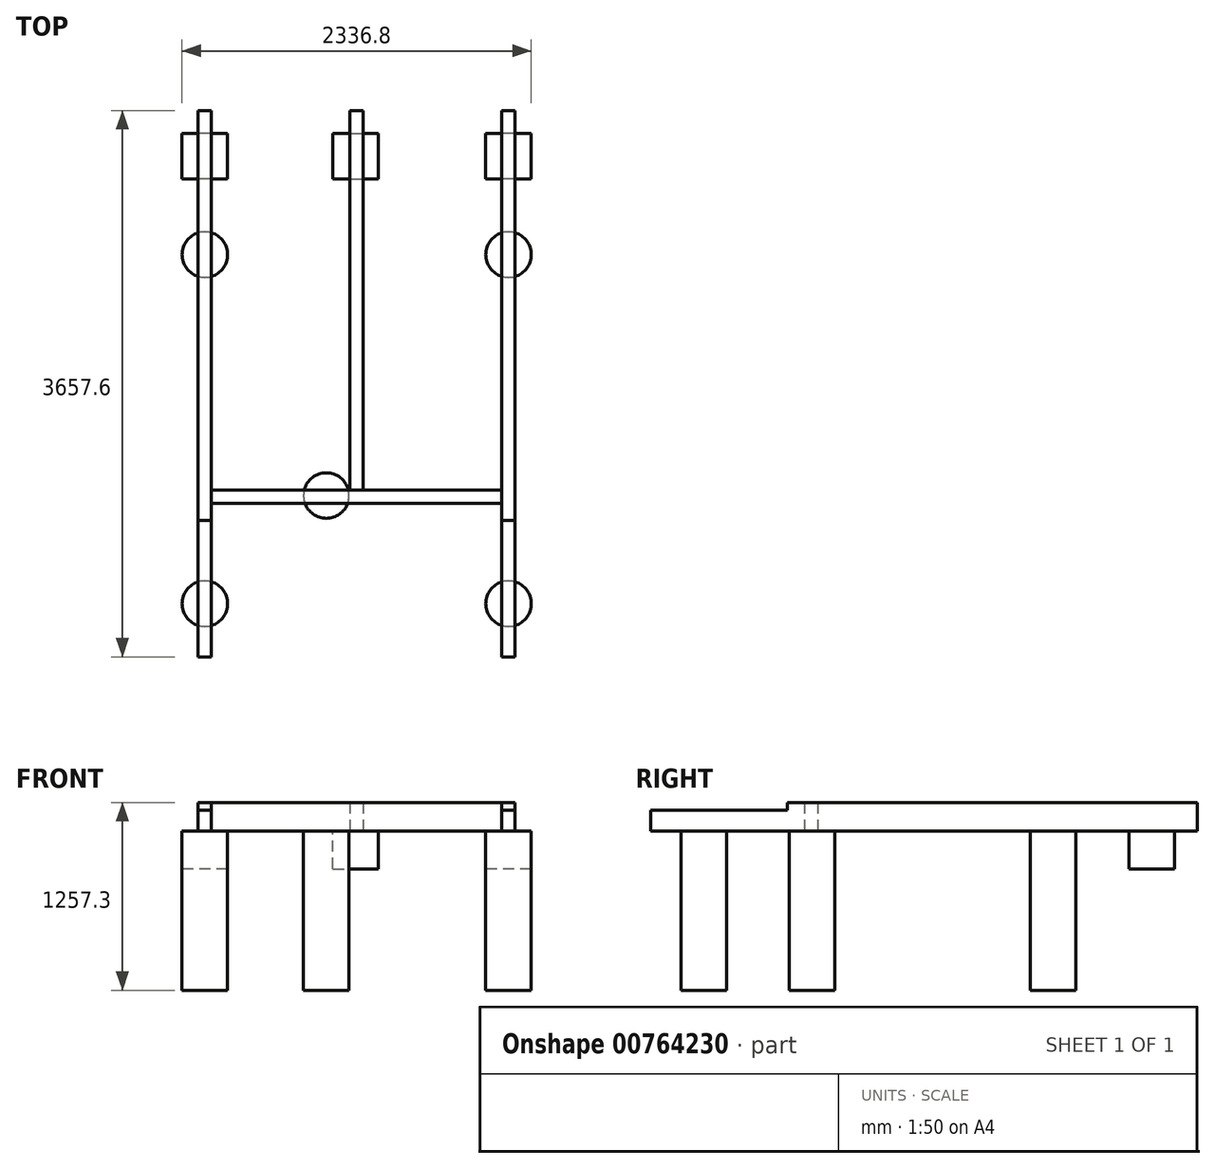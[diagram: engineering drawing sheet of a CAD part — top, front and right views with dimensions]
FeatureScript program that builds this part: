
annotation { "Feature Type Name" : "Feature", "Feature Type Description" : "" }
export const myFeature = defineFeature(function(context is Context, id is Id, definition is map)
    precondition{}
    {
        {
            var Q0;
            Q0=qCreatedBy(makeId("Top.planeOp"),FACE);
            var sketch = newSketch(context, id + "F0", { "sketchPlane" : qUnion([Q0])});
            skLineSegment(sketch, "E0.bottom", {"start": v(-1016, 1828.8) * mm, "end": v(1016, 1828.8) * mm, "construction": true});
            skLineSegment(sketch, "E0.top", {"start": v(-1016, -1828.8) * mm, "end": v(1016, -1828.8) * mm, "construction": true});
            skLineSegment(sketch, "E0.left", {"start": v(-1016, 1828.8) * mm, "end": v(-1016, -1828.8) * mm, "construction": true});
            skLineSegment(sketch, "E0.right", {"start": v(1016, 1828.8) * mm, "end": v(1016, -1828.8) * mm, "construction": true});
            skPoint(sketch, "E0.middle", {"position": v(0, 0) * mm});
            skLineSegment(sketch, "E1.left", {"start": v(-1034.42, -1828.8) * mm, "end": v(-1034.42, -1828.8) * mm});
            skLineSegment(sketch, "E1.right", {"start": v(-997.58, -1828.8) * mm, "end": v(-997.58, -1828.8) * mm});
            skPoint(sketch, "E1.middle", {"position": v(-1016, -1828.8) * mm});
            skPoint(sketch, "E2", {"position": v(1016, 1828.8) * mm});
            skPoint(sketch, "E3", {"position": v(1016, -1828.8) * mm});
            skPoint(sketch, "E4", {"position": v(0, 1828.8) * mm});
            skPoint(sketch, "E5", {"position": v(0, -1828.8) * mm});
            skPoint(sketch, "E6", {"position": v(-1016, 1828.8) * mm});
            skLineSegment(sketch, "E7.bottom", {"start": v(-971.55, -1828.8) * mm, "end": v(-1060.45, -1828.8) * mm});
            skLineSegment(sketch, "E7.top", {"start": v(-971.55, 1828.8) * mm, "end": v(-1060.45, 1828.8) * mm});
            skLineSegment(sketch, "E7.left", {"start": v(-971.55, -1828.8) * mm, "end": v(-971.55, 1828.8) * mm});
            skLineSegment(sketch, "E7.right", {"start": v(-1060.45, -1828.8) * mm, "end": v(-1060.45, 1828.8) * mm});
            skPoint(sketch, "E7.middle", {"position": v(-1016, 0) * mm});
            skPoint(sketch, "E8", {"position": v(1016, 0) * mm});
            skLineSegment(sketch, "E9.bottom", {"start": v(971.55, 1828.8) * mm, "end": v(1060.45, 1828.8) * mm});
            skLineSegment(sketch, "E9.top", {"start": v(971.55, -1828.8) * mm, "end": v(1060.45, -1828.8) * mm});
            skLineSegment(sketch, "E9.left", {"start": v(971.55, 1828.8) * mm, "end": v(971.55, -1828.8) * mm});
            skLineSegment(sketch, "E9.right", {"start": v(1060.45, 1828.8) * mm, "end": v(1060.45, -1828.8) * mm});
            skPoint(sketch, "E10.positionSnap0", {"position": v(1060.45, 0) * mm});
            skLineSegment(sketch, "E11.bottom", {"start": v(-44.45, 1828.8) * mm, "end": v(44.45, 1828.8) * mm});
            skLineSegment(sketch, "E11.top", {"start": v(-44.45, -711.2) * mm, "end": v(44.45, -711.2) * mm});
            skLineSegment(sketch, "E11.left", {"start": v(-44.45, 1828.8) * mm, "end": v(-44.45, -711.2) * mm});
            skLineSegment(sketch, "E11.right", {"start": v(44.45, 1828.8) * mm, "end": v(44.45, -711.2) * mm});
            skLineSegment(sketch, "E12.bottom", {"start": v(-971.55, -711.2) * mm, "end": v(971.55, -711.2) * mm});
            skLineSegment(sketch, "E12.top", {"start": v(-971.55, -800.1) * mm, "end": v(971.55, -800.1) * mm});
            skLineSegment(sketch, "E12.left", {"start": v(-971.55, -711.2) * mm, "end": v(-971.55, -800.1) * mm});
            skLineSegment(sketch, "E12.right", {"start": v(971.55, -711.2) * mm, "end": v(971.55, -800.1) * mm});
            skSolve(sketch);
        }
        {
            var Q0;
            Q0=makeQuery(id+"F0.imprint","IMPRINT",FACE,{"disambiguationData":[TD([[makeQuery(id+"F0.imprint","IMPRINT",EDGE,{"derivedFrom":sQuery(id+"F0.wireOp",EDGE,"E7.bottom")}),-1.0]])]});
            extrude(context, id + "F1", {"entities" : qUnion([Q0]), "depth" : 190.5 * mm, "offsetDistance" : 25.4 * mm});
        }
        {
            var Q0;
            Q0=makeQuery(id+"F0.imprint","IMPRINT",FACE,{"disambiguationData":[TD([[makeQuery(id+"F0.imprint","IMPRINT",EDGE,{"derivedFrom":sQuery(id+"F0.wireOp",EDGE,"E9.bottom")}),-1.0]])]});
            extrude(context, id + "F2", {"entities" : qUnion([Q0]), "depth" : 190.5 * mm, "offsetDistance" : 25.4 * mm});
        }
        {
            var Q0;
            Q0=makeQuery(id+"F0.imprint","IMPRINT",FACE,{"disambiguationData":[TD([[makeQuery(id+"F0.imprint","IMPRINT",EDGE,{"derivedFrom":sQuery(id+"F0.wireOp",EDGE,"E11.bottom")}),-1.0]])]});
            extrude(context, id + "F3", {"entities" : qUnion([Q0]), "depth" : 190.5 * mm, "offsetDistance" : 25.4 * mm});
        }
        {
            var Q0;
            Q0=makeQuery(id+"F2.opExtrude","SWEPT_FACE",FACE,{"disambiguationData":[OSD([sQuery(id+"F0.wireOp",EDGE,"E9.right")])]});
            var sketch = newSketch(context, id + "F4", { "sketchPlane" : qUnion([Q0])});
            skLineSegment(sketch, "E13.bottom", {"start": v(-1828.8, 190.5) * mm, "end": v(-914.4, 190.5) * mm});
            skLineSegment(sketch, "E13.top", {"start": v(-1828.8, 139.7) * mm, "end": v(-914.4, 139.7) * mm});
            skLineSegment(sketch, "E13.left", {"start": v(-1828.8, 190.5) * mm, "end": v(-1828.8, 139.7) * mm});
            skLineSegment(sketch, "E13.right", {"start": v(-914.4, 190.5) * mm, "end": v(-914.4, 139.7) * mm});
            skSolve(sketch);
        }
        {
            var Q0;
            Q0=makeQuery(id+"F1.opExtrude","SWEPT_FACE",FACE,{"disambiguationData":[OSD([sQuery(id+"F0.wireOp",EDGE,"E7.right")])]});
            var sketch = newSketch(context, id + "F5", { "sketchPlane" : qUnion([Q0])});
            skLineSegment(sketch, "E14.bottom", {"start": v(1828.8, 190.5) * mm, "end": v(914.4, 190.5) * mm});
            skLineSegment(sketch, "E14.top", {"start": v(1828.8, 139.7) * mm, "end": v(914.4, 139.7) * mm});
            skLineSegment(sketch, "E14.left", {"start": v(1828.8, 190.5) * mm, "end": v(1828.8, 139.7) * mm});
            skLineSegment(sketch, "E14.right", {"start": v(914.4, 190.5) * mm, "end": v(914.4, 139.7) * mm});
            skSolve(sketch);
        }
        {
            var Q0;
            Q0=makeQuery(id+"F5.imprint","IMPRINT",FACE,{"disambiguationData":[TD([[makeQuery(id+"F5.imprint","IMPRINT",EDGE,{"derivedFrom":sQuery(id+"F5.wireOp",EDGE,"E14.bottom")}),1.0]])]});
            extrude(context, id + "F6", {"entities" : qUnion([Q0]), "operationType" : NewBodyOperationType.REMOVE, "endBound" : BoundingType.THROUGH_ALL, "oppositeDirection" : true, "depth" : 25.4 * mm, "offsetDistance" : 25.4 * mm});
        }
        {
            var Q0;
            Q0=makeQuery(id+"F4.imprint","IMPRINT",FACE,{"disambiguationData":[TD([[makeQuery(id+"F4.imprint","IMPRINT",EDGE,{"derivedFrom":sQuery(id+"F4.wireOp",EDGE,"E13.bottom")}),1.0]])]});
            extrude(context, id + "F7", {"entities" : qUnion([Q0]), "operationType" : NewBodyOperationType.REMOVE, "endBound" : BoundingType.THROUGH_ALL, "oppositeDirection" : true, "depth" : 25.4 * mm, "offsetDistance" : 25.4 * mm});
        }
        {
            var Q0;
            Q0=makeQuery(id+"F3.opExtrude","CAP_FACE",FACE,{"disambiguationData":[OSD([sQuery(id+"F0.wireOp",EDGE,"E11.bottom"),sQuery(id+"F0.wireOp",EDGE,"E11.top"),sQuery(id+"F0.wireOp",EDGE,"E11.left"),sQuery(id+"F0.wireOp",EDGE,"E11.right")])],"isStart":true});
            var sketch = newSketch(context, id + "F8", { "sketchPlane" : qUnion([Q0])});
            skLineSegment(sketch, "E15", {"start": v(-1060.45, 1828.8) * mm, "end": v(-971.55, 1828.8) * mm, "construction": true});
            skLineSegment(sketch, "E16", {"start": v(971.55, 1828.8) * mm, "end": v(1060.45, 1828.8) * mm, "construction": true});
            skPoint(sketch, "E17", {"position": v(1016, 1828.8) * mm});
            skPoint(sketch, "E18", {"position": v(-1016, 1828.8) * mm});
            skLineSegment(sketch, "E19", {"start": v(-1060.45, -1828.8) * mm, "end": v(-971.55, -1828.8) * mm, "construction": true});
            skPoint(sketch, "E20", {"position": v(-1016, -1828.8) * mm});
            skLineSegment(sketch, "E21", {"start": v(-44.45, -1828.8) * mm, "end": v(44.45, -1828.8) * mm, "construction": true});
            skPoint(sketch, "E22", {"position": v(0, -1828.8) * mm});
            skLineSegment(sketch, "E23", {"start": v(971.55, -1828.8) * mm, "end": v(1060.45, -1828.8) * mm, "construction": true});
            skPoint(sketch, "E24", {"position": v(1016, -1828.8) * mm});
            skLineSegment(sketch, "E25", {"start": v(1016, -1828.8) * mm, "end": v(1016, 1828.8) * mm, "construction": true});
            skLineSegment(sketch, "E26", {"start": v(0, -1828.8) * mm, "end": v(0, -1828.8) * mm});
            skLineSegment(sketch, "E27", {"start": v(-1016, 1828.8) * mm, "end": v(-1016, -1828.8) * mm, "construction": true});
            skCircle(sketch, "E28", {"center": v(-1016, 1473.2) * mm, "radius": 152.4 * mm});
            skCircle(sketch, "E29", {"center": v(1016, 1473.2) * mm, "radius": 152.4 * mm});
            skCircle(sketch, "E30", {"center": v(1016, -863.6) * mm, "radius": 152.4 * mm});
            skCircle(sketch, "E31", {"center": v(-1016, -863.6) * mm, "radius": 152.4 * mm});
            skCircle(sketch, "E32", {"center": v(-203.2, 749.3) * mm, "radius": 152.4 * mm});
            skLineSegment(sketch, "E33.bottom", {"start": v(-863.6, -1676.4) * mm, "end": v(-1168.4, -1676.4) * mm});
            skLineSegment(sketch, "E33.top", {"start": v(-863.6, -1371.6) * mm, "end": v(-1168.4, -1371.6) * mm});
            skLineSegment(sketch, "E33.left", {"start": v(-863.6, -1676.4) * mm, "end": v(-863.6, -1371.6) * mm});
            skLineSegment(sketch, "E33.right", {"start": v(-1168.4, -1676.4) * mm, "end": v(-1168.4, -1371.6) * mm});
            skPoint(sketch, "E33.middle", {"position": v(-1016, -1524) * mm});
            skLineSegment(sketch, "E34.bottom", {"start": v(-158.75, -1676.4) * mm, "end": v(146.05, -1676.4) * mm});
            skLineSegment(sketch, "E34.top", {"start": v(-158.75, -1371.6) * mm, "end": v(146.05, -1371.6) * mm});
            skLineSegment(sketch, "E34.left", {"start": v(-158.75, -1676.4) * mm, "end": v(-158.75, -1371.6) * mm});
            skLineSegment(sketch, "E34.right", {"start": v(146.05, -1676.4) * mm, "end": v(146.05, -1371.6) * mm});
            skPoint(sketch, "E34.middle", {"position": v(-6.35, -1524) * mm});
            skLineSegment(sketch, "E35.bottom", {"start": v(1168.4, -1676.4) * mm, "end": v(863.6, -1676.4) * mm});
            skLineSegment(sketch, "E35.top", {"start": v(1168.4, -1371.6) * mm, "end": v(863.6, -1371.6) * mm});
            skLineSegment(sketch, "E35.left", {"start": v(1168.4, -1676.4) * mm, "end": v(1168.4, -1371.6) * mm});
            skLineSegment(sketch, "E35.right", {"start": v(863.6, -1676.4) * mm, "end": v(863.6, -1371.6) * mm});
            skPoint(sketch, "E35.middle", {"position": v(1016, -1524) * mm});
            skLineSegment(sketch, "E36.bottom", {"start": v(-355.6, 901.7) * mm, "end": v(-50.8, 901.7) * mm});
            skLineSegment(sketch, "E36.top", {"start": v(-355.6, 596.9) * mm, "end": v(-50.8, 596.9) * mm});
            skLineSegment(sketch, "E36.left", {"start": v(-355.6, 901.7) * mm, "end": v(-355.6, 596.9) * mm});
            skLineSegment(sketch, "E36.right", {"start": v(-50.8, 901.7) * mm, "end": v(-50.8, 596.9) * mm});
            skLineSegment(sketch, "E37.bottom", {"start": v(-863.6, 406.4) * mm, "end": v(-1168.4, 406.4) * mm});
            skLineSegment(sketch, "E37.top", {"start": v(-863.6, 711.2) * mm, "end": v(-1168.4, 711.2) * mm});
            skLineSegment(sketch, "E37.left", {"start": v(-863.6, 406.4) * mm, "end": v(-863.6, 711.2) * mm});
            skLineSegment(sketch, "E37.right", {"start": v(-1168.4, 406.4) * mm, "end": v(-1168.4, 711.2) * mm});
            skPoint(sketch, "E37.middle", {"position": v(-1016, 558.8) * mm});
            skLineSegment(sketch, "E38.bottom", {"start": v(863.6, 406.4) * mm, "end": v(1168.4, 406.4) * mm});
            skLineSegment(sketch, "E38.top", {"start": v(863.6, 711.2) * mm, "end": v(1168.4, 711.2) * mm});
            skLineSegment(sketch, "E38.left", {"start": v(863.6, 406.4) * mm, "end": v(863.6, 711.2) * mm});
            skLineSegment(sketch, "E38.right", {"start": v(1168.4, 406.4) * mm, "end": v(1168.4, 711.2) * mm});
            skPoint(sketch, "E38.middle", {"position": v(1016, 558.8) * mm});
            skLineSegment(sketch, "E39.bottom", {"start": v(-762, 304.8) * mm, "end": v(-1270, 304.8) * mm});
            skLineSegment(sketch, "E39.top", {"start": v(-762, 812.8) * mm, "end": v(-1270, 812.8) * mm});
            skLineSegment(sketch, "E39.left", {"start": v(-762, 304.8) * mm, "end": v(-762, 812.8) * mm});
            skLineSegment(sketch, "E39.right", {"start": v(-1270, 304.8) * mm, "end": v(-1270, 812.8) * mm});
            skLineSegment(sketch, "E40.bottom", {"start": v(762, 304.8) * mm, "end": v(1270, 304.8) * mm});
            skLineSegment(sketch, "E40.top", {"start": v(762, 812.8) * mm, "end": v(1270, 812.8) * mm});
            skLineSegment(sketch, "E40.left", {"start": v(762, 304.8) * mm, "end": v(762, 812.8) * mm});
            skLineSegment(sketch, "E40.right", {"start": v(1270, 304.8) * mm, "end": v(1270, 812.8) * mm});
            skLineSegment(sketch, "E41.bottom", {"start": v(1270, -1270) * mm, "end": v(762, -1270) * mm});
            skLineSegment(sketch, "E41.top", {"start": v(1270, -1778) * mm, "end": v(762, -1778) * mm});
            skLineSegment(sketch, "E41.left", {"start": v(1270, -1270) * mm, "end": v(1270, -1778) * mm});
            skLineSegment(sketch, "E41.right", {"start": v(762, -1270) * mm, "end": v(762, -1778) * mm});
            skLineSegment(sketch, "E42.bottom", {"start": v(247.65, -1270) * mm, "end": v(-260.35, -1270) * mm});
            skLineSegment(sketch, "E42.top", {"start": v(247.65, -1778) * mm, "end": v(-260.35, -1778) * mm});
            skLineSegment(sketch, "E42.left", {"start": v(247.65, -1270) * mm, "end": v(247.65, -1778) * mm});
            skLineSegment(sketch, "E42.right", {"start": v(-260.35, -1270) * mm, "end": v(-260.35, -1778) * mm});
            skLineSegment(sketch, "E43.bottom", {"start": v(-762, -1270) * mm, "end": v(-1270, -1270) * mm});
            skLineSegment(sketch, "E43.top", {"start": v(-762, -1778) * mm, "end": v(-1270, -1778) * mm});
            skLineSegment(sketch, "E43.left", {"start": v(-762, -1270) * mm, "end": v(-762, -1778) * mm});
            skLineSegment(sketch, "E43.right", {"start": v(-1270, -1270) * mm, "end": v(-1270, -1778) * mm});
            skSolve(sketch);
        }
        {
            var Q0;
            Q0=makeQuery(id+"F8.imprint","IMPRINT",FACE,{"disambiguationData":[TD([[makeQuery(id+"F8.imprint","IMPRINT",EDGE,{"derivedFrom":sQuery(id+"F8.wireOp",EDGE,"E28")}),1.0]])]});
            extrude(context, id + "F9", {"entities" : qUnion([Q0]), "depth" : 1066.8 * mm, "offsetDistance" : 25.4 * mm});
        }
        {
            var Q0;
            Q0=makeQuery(id+"F8.imprint","IMPRINT",FACE,{"disambiguationData":[TD([[makeQuery(id+"F8.imprint","IMPRINT",EDGE,{"derivedFrom":sQuery(id+"F8.wireOp",EDGE,"E29")}),1.0]])]});
            extrude(context, id + "F10", {"entities" : qUnion([Q0]), "depth" : 1066.8 * mm, "offsetDistance" : 25.4 * mm});
        }
        {
            var Q0;
            Q0=makeQuery(id+"F8.imprint","IMPRINT",FACE,{"disambiguationData":[TD([[makeQuery(id+"F8.imprint","IMPRINT",EDGE,{"derivedFrom":sQuery(id+"F8.wireOp",EDGE,"E30")}),1.0]])]});
            extrude(context, id + "F11", {"entities" : qUnion([Q0]), "depth" : 1066.8 * mm, "offsetDistance" : 25.4 * mm});
        }
        {
            var Q0;
            Q0=makeQuery(id+"F8.imprint","IMPRINT",FACE,{"disambiguationData":[TD([[makeQuery(id+"F8.imprint","IMPRINT",EDGE,{"derivedFrom":sQuery(id+"F8.wireOp",EDGE,"E31")}),1.0]])]});
            extrude(context, id + "F12", {"entities" : qUnion([Q0]), "depth" : 1066.8 * mm, "offsetDistance" : 25.4 * mm});
        }
        {
            var Q0;
            {var subQ0=sQuery(id+"F8.wireOp",EDGE,"E32");var subQ1=makeQuery(id+"F3.opExtrude","CAP_EDGE",EDGE,{"disambiguationData":[OSD([sQuery(id+"F0.wireOp",EDGE,"E11.top")])],"isStart":true});var subQ2=makeQuery(id+"F8.imprint","INTERSECT",VERTEX,{"derivedFrom":[subQ1,subQ0]});Q0=makeQuery(id+"F8.imprint","IMPRINT",FACE,{"disambiguationData":[TD([[makeQuery(id+"F8.imprint","IMPRINT",EDGE,{"disambiguationData":[TD([[subQ2,-1.0]])],"derivedFrom":subQ0}),1.0]])]});}
            extrude(context, id + "F13", {"entities" : qUnion([Q0]), "depth" : 1066.8 * mm, "offsetDistance" : 25.4 * mm});
        }
        {
            var Q0;
            Q0=makeQuery(id+"F0.imprint","IMPRINT",FACE,{"disambiguationData":[TD([[makeQuery(id+"F0.imprint","IMPRINT",EDGE,{"derivedFrom":sQuery(id+"F0.wireOp",EDGE,"E12.top")}),1.0]])]});
            extrude(context, id + "F14", {"entities" : qUnion([Q0]), "depth" : 190.5 * mm, "offsetDistance" : 25.4 * mm});
        }
        {
            var Q0;
            Q0=makeQuery(id+"F8.imprint","IMPRINT",FACE,{"disambiguationData":[TD([[makeQuery(id+"F8.imprint","IMPRINT",EDGE,{"derivedFrom":sQuery(id+"F8.wireOp",EDGE,"E35.bottom")}),-1.0]])]});
            var Q1;
            Q1=makeQuery(id+"F8.imprint","IMPRINT",FACE,{"disambiguationData":[TD([[makeQuery(id+"F8.imprint","IMPRINT",EDGE,{"derivedFrom":sQuery(id+"F8.wireOp",EDGE,"E33.bottom")}),-1.0]])]});
            var Q2;
            Q2=makeQuery(id+"F8.imprint","IMPRINT",FACE,{"disambiguationData":[TD([[makeQuery(id+"F8.imprint","IMPRINT",EDGE,{"derivedFrom":sQuery(id+"F8.wireOp",EDGE,"E34.bottom")}),1.0]])]});
            extrude(context, id + "F15", {"entities" : qUnion([Q0, Q1, Q2]), "depth" : 254 * mm, "offsetDistance" : 25.4 * mm});
        }
    });
